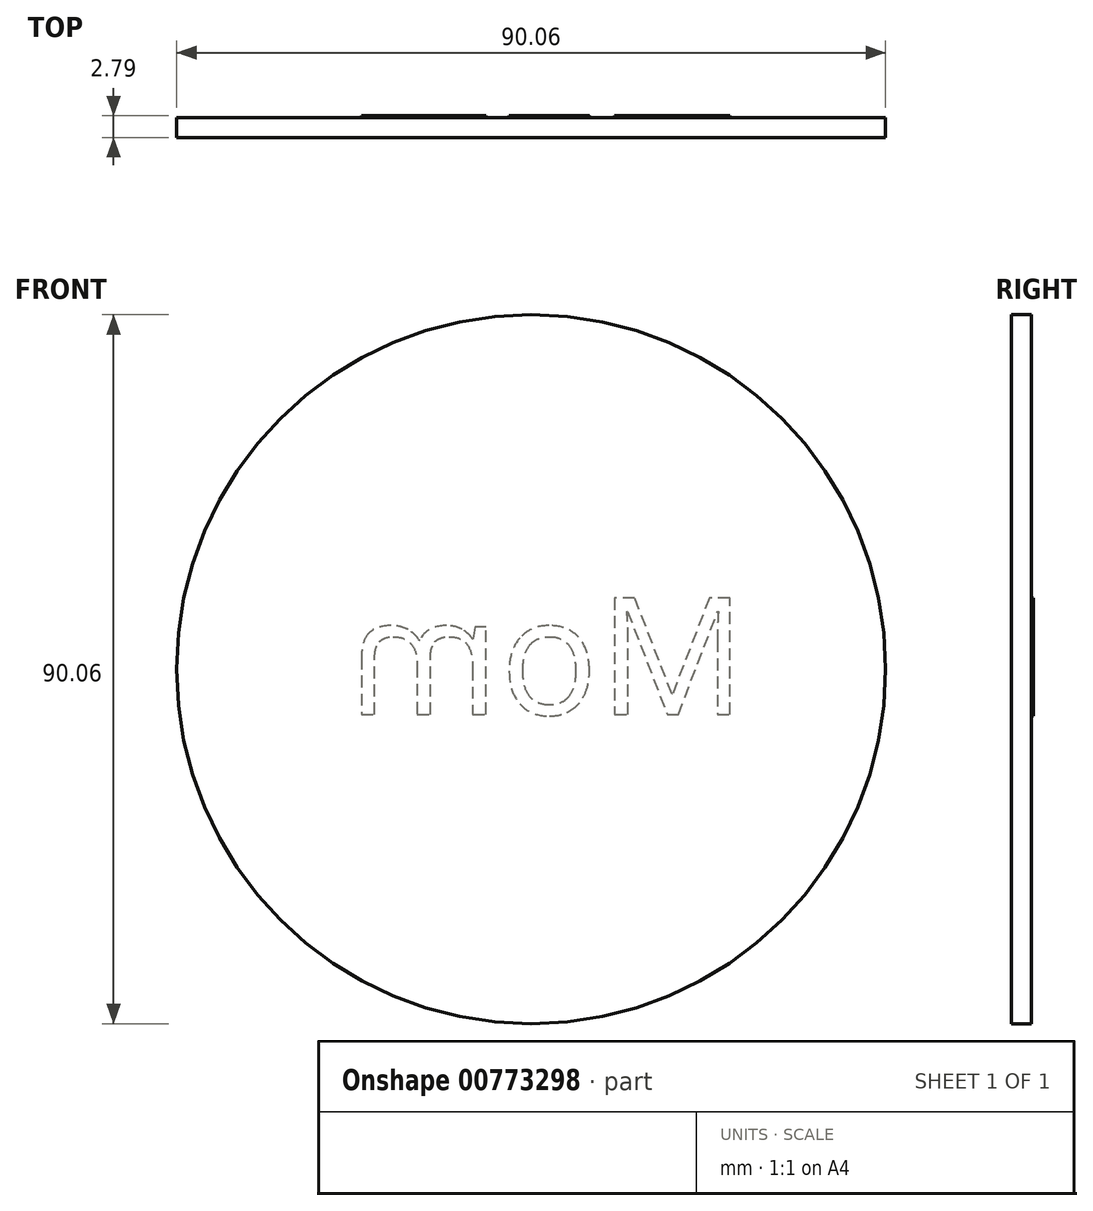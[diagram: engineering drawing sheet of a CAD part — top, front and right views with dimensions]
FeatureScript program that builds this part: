
annotation { "Feature Type Name" : "Feature", "Feature Type Description" : "" }
export const myFeature = defineFeature(function(context is Context, id is Id, definition is map)
    precondition{}
    {
        {
            var Q0;
            Q0=qCreatedBy(makeId("Front.planeOp"),FACE);
            var sketch = newSketch(context, id + "F0", { "sketchPlane" : qUnion([Q0])});
            skCircle(sketch, "E0", {"center": v(0, 0) * mm, "radius": 45.03 * mm});
            skSolve(sketch);
        }
        {
            var Q0;
            Q0 = qSketchRegion(id + "F0", true);
            extrude(context, id + "F1", {"entities" : qUnion([Q0]), "depth" : 2.54 * mm, "offsetDistance" : 25.4 * mm});
        }
        {
            var Q0;
            Q0=makeQuery(id+"F1.opExtrude","CAP_FACE",FACE,{"disambiguationData":[OSD([sQuery(id+"F0.wireOp",EDGE,"E0")])],"isStart":true});
            var sketch = newSketch(context, id + "F2", { "sketchPlane" : qUnion([Q0])});
            skText(sketch, "E1", { "text": "Mom", "fontName": "OpenSans-Regular.ttf"});
            const initialGuessF2  = {"E1": [-0.02727, -0.00575, 1, 0, 0.01492]};
            skSetInitialGuess(sketch, initialGuessF2);
            skSolve(sketch);
        }
        {
            var Q0;
            Q0 = qSketchRegion(id + "F2", true);
            extrude(context, id + "F3", {"entities" : qUnion([Q0]), "operationType" : NewBodyOperationType.ADD, "depth" : 0.25 * mm, "offsetDistance" : 25.4 * mm});
        }
    });
